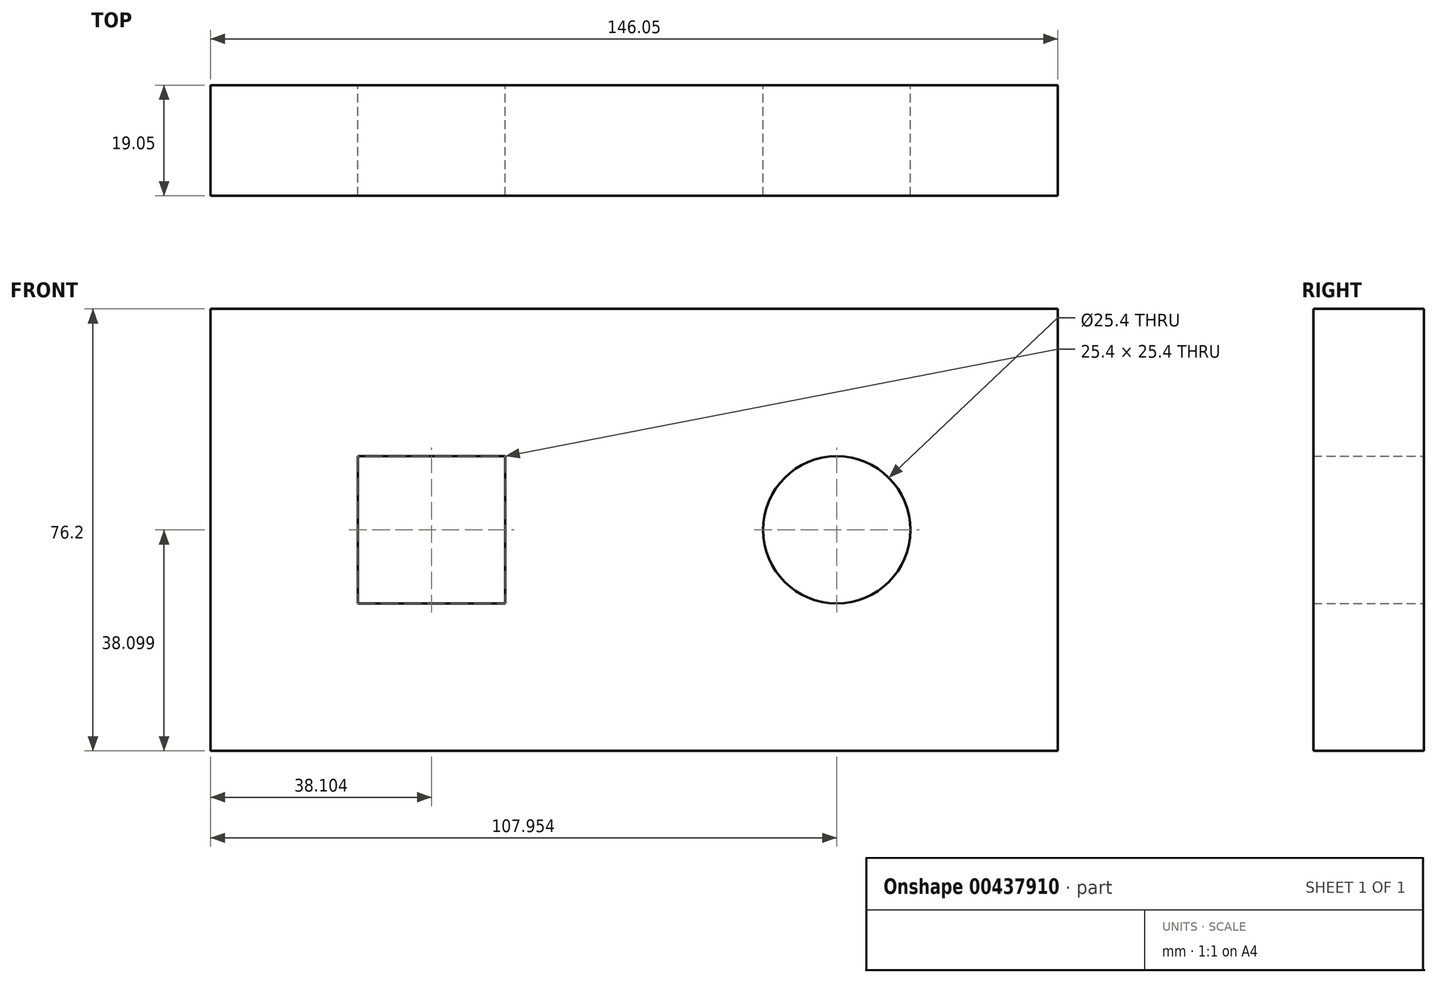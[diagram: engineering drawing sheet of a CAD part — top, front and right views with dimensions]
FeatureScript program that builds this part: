
annotation { "Feature Type Name" : "Feature", "Feature Type Description" : "" }
export const myFeature = defineFeature(function(context is Context, id is Id, definition is map)
    precondition{}
    {
        {
            var Q0;
            Q0=qCreatedBy(makeId("Front.planeOp"),FACE);
            var sketch = newSketch(context, id + "F0", { "sketchPlane" : qUnion([Q0])});
            skLineSegment(sketch, "E0.bottom", {"start": v(-73.14, 43.99) * mm, "end": v(72.91, 43.99) * mm});
            skLineSegment(sketch, "E0.top", {"start": v(-73.14, -32.21) * mm, "end": v(72.91, -32.21) * mm});
            skLineSegment(sketch, "E0.left", {"start": v(-73.14, 43.99) * mm, "end": v(-73.14, -32.21) * mm});
            skLineSegment(sketch, "E0.right", {"start": v(72.91, 43.99) * mm, "end": v(72.91, -32.21) * mm});
            skCircle(sketch, "E1", {"center": v(34.81, 5.89) * mm, "radius": 12.7 * mm});
            skLineSegment(sketch, "E2.bottom", {"start": v(-47.74, 18.59) * mm, "end": v(-22.34, 18.59) * mm});
            skLineSegment(sketch, "E2.top", {"start": v(-47.74, -6.81) * mm, "end": v(-22.34, -6.81) * mm});
            skLineSegment(sketch, "E2.left", {"start": v(-47.74, 18.59) * mm, "end": v(-47.74, -6.81) * mm});
            skLineSegment(sketch, "E2.right", {"start": v(-22.34, 18.59) * mm, "end": v(-22.34, -6.81) * mm});
            skSolve(sketch);
        }
        {
            var Q0;
            Q0 = qSketchRegion(id + "F0", true);
            extrude(context, id + "F1", {"entities" : qUnion([Q0]), "depth" : 19.05 * mm});
        }
    });
